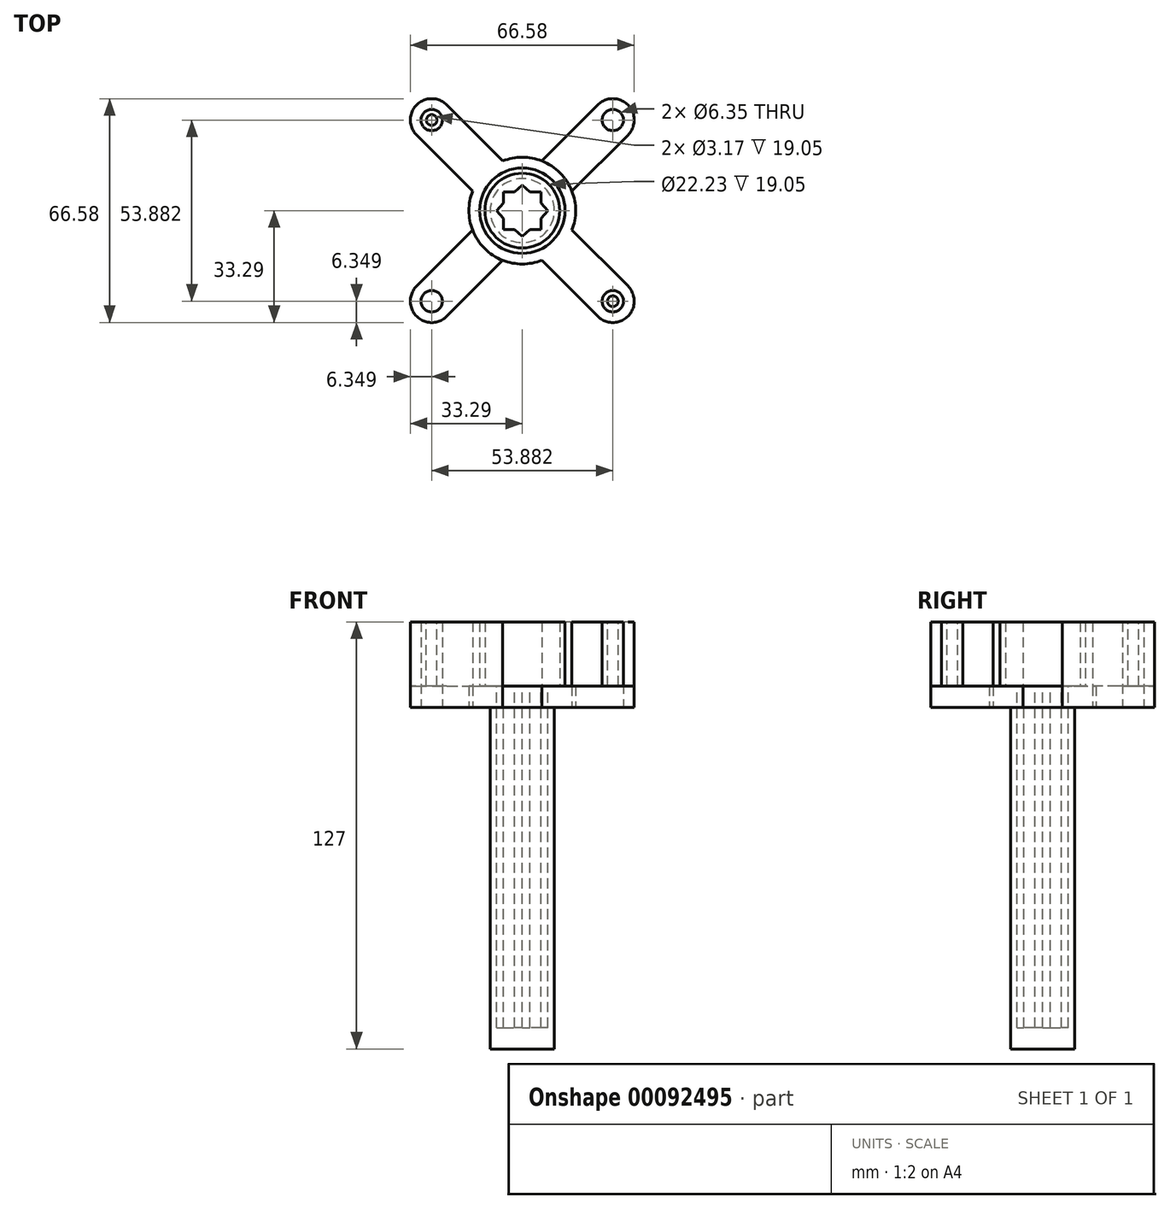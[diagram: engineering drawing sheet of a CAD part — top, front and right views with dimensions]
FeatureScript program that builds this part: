
annotation { "Feature Type Name" : "Feature", "Feature Type Description" : "" }
export const myFeature = defineFeature(function(context is Context, id is Id, definition is map)
    precondition{}
    {
        {
            var Q0;
            Q0=qCreatedBy(makeId("Top.planeOp"),FACE);
            var sketch = newSketch(context, id + "F0", { "sketchPlane" : qUnion([Q0])});
            skCircle(sketch, "E0", {"center": v(0, 0) * mm, "radius": 9.53 * mm});
            skSolve(sketch);
        }
        {
            var Q0;
            Q0 = qSketchRegion(id + "F0", true);
            extrude(context, id + "F1", {"entities" : qUnion([Q0]), "endBound" : BoundingType.SYMMETRIC, "depth" : 101.6 * mm});
        }
        {
            var Q0;
            Q0=makeQuery(id+"F1.opExtrude","CAP_FACE",FACE,{"disambiguationData":[OSD([sQuery(id+"F0.wireOp",EDGE,"E0")])],"isStart":false});
            var sketch = newSketch(context, id + "F2", { "sketchPlane" : qUnion([Q0])});
            skCircle(sketch, "E1", {"center": v(0, 0) * mm, "radius": 15.88 * mm});
            skLineSegment(sketch, "E2", {"start": v(-22.45, 31.43) * mm, "end": v(-5.8, 14.78) * mm});
            skLineSegment(sketch, "E3", {"start": v(-31.43, 22.45) * mm, "end": v(-14.78, 5.8) * mm});
            skLineSegment(sketch, "E4.MirrorCS", {"start": v(31.43, -22.45) * mm, "end": v(14.78, -5.8) * mm});
            skLineSegment(sketch, "E5.MirrorCS", {"start": v(22.45, -31.43) * mm, "end": v(5.8, -14.78) * mm});
            skLineSegment(sketch, "E6", {"start": v(31.43, 22.45) * mm, "end": v(14.78, 5.8) * mm});
            skLineSegment(sketch, "E7.MirrorCS", {"start": v(22.45, 31.43) * mm, "end": v(5.8, 14.78) * mm});
            skLineSegment(sketch, "E8.MirrorCS", {"start": v(-22.45, -31.43) * mm, "end": v(-5.8, -14.78) * mm});
            skLineSegment(sketch, "E9.MirrorCS", {"start": v(-31.43, -22.45) * mm, "end": v(-14.78, -5.8) * mm});
            skArc(sketch, "E10", {"start": v(31.43, 22.45) * mm, "mid": v(31.43, 31.43) * mm, "end": v(22.45, 31.43) * mm});
            skArc(sketch, "E11.MirrorCS", {"start": v(-31.43, 22.45) * mm, "mid": v(-31.43, 31.43) * mm, "end": v(-22.45, 31.43) * mm});
            skArc(sketch, "E12.MirrorCS", {"start": v(-31.43, -22.45) * mm, "mid": v(-31.43, -31.43) * mm, "end": v(-22.45, -31.43) * mm});
            skArc(sketch, "E13.MirrorCS", {"start": v(31.43, -22.45) * mm, "mid": v(31.43, -31.43) * mm, "end": v(22.45, -31.43) * mm});
            skCircle(sketch, "E14", {"center": v(-26.94, 26.94) * mm, "radius": 3.18 * mm});
            skCircle(sketch, "E15.MirrorC", {"center": v(-26.94, -26.94) * mm, "radius": 3.18 * mm});
            skCircle(sketch, "E16.MirrorC", {"center": v(26.94, 26.94) * mm, "radius": 3.18 * mm});
            skCircle(sketch, "E17.MirrorC", {"center": v(26.94, -26.94) * mm, "radius": 3.18 * mm});
            skSolve(sketch);
        }
        {
            var Q0;
            {var subQ0=sQuery(id+"F2.wireOp",EDGE,"E6");Q0=makeQuery(id+"F2.imprint","IMPRINT",FACE,{"disambiguationData":[TD([[makeQuery(id+"F2.imprint","IMPRINT",EDGE,{"derivedFrom":subQ0}),-1.0]])]});}
            var Q1;
            {var subQ0=sQuery(id+"F2.wireOp",EDGE,"E8.MirrorCS");Q1=makeQuery(id+"F2.imprint","IMPRINT",FACE,{"disambiguationData":[TD([[makeQuery(id+"F2.imprint","IMPRINT",EDGE,{"derivedFrom":subQ0}),1.0]])]});}
            var Q2;
            {var subQ0=sQuery(id+"F2.wireOp",EDGE,"E4.MirrorCS");Q2=makeQuery(id+"F2.imprint","IMPRINT",FACE,{"disambiguationData":[TD([[makeQuery(id+"F2.imprint","IMPRINT",EDGE,{"derivedFrom":subQ0}),1.0]])]});}
            var Q3;
            Q3=makeQuery(id+"F2.imprint","IMPRINT",FACE,{"disambiguationData":[TD([[makeQuery(id+"F2.imprint","IMPRINT",EDGE,{"derivedFrom":makeQuery(id+"F1.opExtrude","CAP_EDGE",EDGE,{"disambiguationData":[OSD([sQuery(id+"F0.wireOp",EDGE,"E0")])],"isStart":false})}),1.0]])]});
            var Q4;
            Q4=makeQuery(id+"F2.imprint","IMPRINT",FACE,{"disambiguationData":[TD([[makeQuery(id+"F2.imprint","IMPRINT",EDGE,{"derivedFrom":makeQuery(id+"F1.opExtrude","CAP_EDGE",EDGE,{"disambiguationData":[OSD([sQuery(id+"F0.wireOp",EDGE,"E0")])],"isStart":false})}),-1.0]])]});
            var Q5;
            {var subQ0=sQuery(id+"F2.wireOp",EDGE,"E2");Q5=makeQuery(id+"F2.imprint","IMPRINT",FACE,{"disambiguationData":[TD([[makeQuery(id+"F2.imprint","IMPRINT",EDGE,{"derivedFrom":subQ0}),-1.0]])]});}
            extrude(context, id + "F3", {"entities" : qUnion([Q0, Q1, Q2, Q3, Q4, Q5]), "operationType" : NewBodyOperationType.ADD, "depth" : 6.35 * mm});
        }
        {
            var Q0;
            Q0=makeQuery(id+"F2.imprint","IMPRINT",FACE,{"disambiguationData":[TD([[makeQuery(id+"F2.imprint","IMPRINT",EDGE,{"derivedFrom":sQuery(id+"F2.wireOp",EDGE,"E14")}),1.0]])]});
            var Q1;
            Q1=makeQuery(id+"F2.imprint","IMPRINT",FACE,{"disambiguationData":[TD([[makeQuery(id+"F2.imprint","IMPRINT",EDGE,{"derivedFrom":sQuery(id+"F2.wireOp",EDGE,"E16.MirrorC")}),-1.0]])]});
            var Q2;
            Q2=makeQuery(id+"F2.imprint","IMPRINT",FACE,{"disambiguationData":[TD([[makeQuery(id+"F2.imprint","IMPRINT",EDGE,{"derivedFrom":sQuery(id+"F2.wireOp",EDGE,"E17.MirrorC")}),1.0]])]});
            var Q3;
            Q3=makeQuery(id+"F2.imprint","IMPRINT",FACE,{"disambiguationData":[TD([[makeQuery(id+"F2.imprint","IMPRINT",EDGE,{"derivedFrom":sQuery(id+"F2.wireOp",EDGE,"E15.MirrorC")}),-1.0]])]});
            extrude(context, id + "F4", {"entities" : qUnion([Q0, Q1, Q2, Q3]), "operationType" : NewBodyOperationType.ADD, "depth" : 25.4 * mm});
        }
        {
            var Q0;
            Q0=makeQuery(id+"F3.opExtrude","CAP_FACE",FACE,{"disambiguationData":[OSD([sQuery(id+"F2.wireOp",EDGE,"E1"),sQuery(id+"F2.wireOp",EDGE,"E2"),sQuery(id+"F2.wireOp",EDGE,"E3"),sQuery(id+"F2.wireOp",EDGE,"E4.MirrorCS"),sQuery(id+"F2.wireOp",EDGE,"E5.MirrorCS"),sQuery(id+"F2.wireOp",EDGE,"E6"),sQuery(id+"F2.wireOp",EDGE,"E7.MirrorCS"),sQuery(id+"F2.wireOp",EDGE,"E8.MirrorCS"),sQuery(id+"F2.wireOp",EDGE,"E9.MirrorCS"),sQuery(id+"F2.wireOp",EDGE,"E10"),sQuery(id+"F2.wireOp",EDGE,"E11.MirrorCS"),sQuery(id+"F2.wireOp",EDGE,"E12.MirrorCS"),sQuery(id+"F2.wireOp",EDGE,"E13.MirrorCS"),sQuery(id+"F2.wireOp",EDGE,"E14"),sQuery(id+"F2.wireOp",EDGE,"E15.MirrorC"),sQuery(id+"F2.wireOp",EDGE,"E16.MirrorC"),sQuery(id+"F2.wireOp",EDGE,"E17.MirrorC")])],"isStart":false});
            var sketch = newSketch(context, id + "F5", { "sketchPlane" : qUnion([Q0])});
            skLineSegment(sketch, "E18", {"start": v(-7.62, 0) * mm, "end": v(-7.62, 7.62) * mm});
            skLineSegment(sketch, "E19", {"start": v(-7.62, 7.62) * mm, "end": v(0, 7.62) * mm});
            skLineSegment(sketch, "E20", {"start": v(0, 7.62) * mm, "end": v(-2.28, 5.6) * mm});
            skLineSegment(sketch, "E21", {"start": v(-7.62, 0) * mm, "end": v(-5.6, 2.28) * mm});
            skLineSegment(sketch, "E22", {"start": v(-5.6, 2.28) * mm, "end": v(-5.6, 5.6) * mm});
            skLineSegment(sketch, "E23", {"start": v(-5.6, 5.6) * mm, "end": v(-2.28, 5.6) * mm});
            skLineSegment(sketch, "E24.MirrorCS", {"start": v(7.62, 7.62) * mm, "end": v(0, 7.62) * mm});
            skLineSegment(sketch, "E25.MirrorCS", {"start": v(0, 7.62) * mm, "end": v(2.28, 5.6) * mm});
            skLineSegment(sketch, "E26.MirrorCS", {"start": v(5.6, 5.6) * mm, "end": v(2.28, 5.6) * mm});
            skLineSegment(sketch, "E27.MirrorCS", {"start": v(5.6, 2.28) * mm, "end": v(5.6, 5.6) * mm});
            skLineSegment(sketch, "E28.MirrorCS", {"start": v(7.62, 0) * mm, "end": v(5.6, 2.28) * mm});
            skLineSegment(sketch, "E29.MirrorCS", {"start": v(7.62, 0) * mm, "end": v(7.62, 7.62) * mm});
            skLineSegment(sketch, "E30.MirrorCS", {"start": v(-7.62, 0) * mm, "end": v(-5.6, -2.28) * mm});
            skLineSegment(sketch, "E31.MirrorCS", {"start": v(-5.6, -2.28) * mm, "end": v(-5.6, -5.6) * mm});
            skLineSegment(sketch, "E32.MirrorCS", {"start": v(-5.6, -5.6) * mm, "end": v(-2.28, -5.6) * mm});
            skLineSegment(sketch, "E33.MirrorCS", {"start": v(0, -7.62) * mm, "end": v(-2.28, -5.6) * mm});
            skLineSegment(sketch, "E34.MirrorCS", {"start": v(0, -7.62) * mm, "end": v(2.28, -5.6) * mm});
            skLineSegment(sketch, "E35.MirrorCS", {"start": v(5.6, -5.6) * mm, "end": v(2.28, -5.6) * mm});
            skLineSegment(sketch, "E36.MirrorCS", {"start": v(5.6, -2.28) * mm, "end": v(5.6, -5.6) * mm});
            skLineSegment(sketch, "E37.MirrorCS", {"start": v(7.62, 0) * mm, "end": v(5.6, -2.28) * mm});
            skLineSegment(sketch, "E38.MirrorCS", {"start": v(7.62, 0) * mm, "end": v(7.62, -7.62) * mm});
            skLineSegment(sketch, "E39.MirrorCS", {"start": v(7.62, -7.62) * mm, "end": v(0, -7.62) * mm});
            skLineSegment(sketch, "E40.MirrorCS", {"start": v(-7.62, -7.62) * mm, "end": v(0, -7.62) * mm});
            skLineSegment(sketch, "E41.MirrorCS", {"start": v(-7.62, 0) * mm, "end": v(-7.62, -7.62) * mm});
            skCircle(sketch, "E42", {"center": v(0, 0) * mm, "radius": 11.11 * mm});
            skCircle(sketch, "E43", {"center": v(0, 0) * mm, "radius": 12.7 * mm});
            skSolve(sketch);
        }
        {
            var Q0;
            Q0=makeQuery(id+"F5.imprint","IMPRINT",FACE,{"disambiguationData":[TD([[makeQuery(id+"F5.imprint","IMPRINT",EDGE,{"derivedFrom":sQuery(id+"F5.wireOp",EDGE,"E20")}),1.0]])]});
            extrude(context, id + "F6", {"entities" : qUnion([Q0]), "operationType" : NewBodyOperationType.REMOVE, "oppositeDirection" : true, "depth" : 101.6 * mm});
        }
        {
            var Q0;
            Q0=makeQuery(id+"F5.imprint","IMPRINT",FACE,{"disambiguationData":[TD([[makeQuery(id+"F5.imprint","IMPRINT",EDGE,{"derivedFrom":sQuery(id+"F5.wireOp",EDGE,"E42")}),-1.0]])]});
            extrude(context, id + "F7", {"entities" : qUnion([Q0]), "operationType" : NewBodyOperationType.ADD, "depth" : 19.05 * mm});
        }
        {
            var Q0;
            Q0=makeQuery(id+"F4.opExtrude","CAP_FACE",FACE,{"disambiguationData":[OSD([sQuery(id+"F2.wireOp",EDGE,"E17.MirrorC")])],"isStart":false});
            var sketch = newSketch(context, id + "F8", { "sketchPlane" : qUnion([Q0])});
            skCircle(sketch, "E44", {"center": v(26.94, -26.94) * mm, "radius": 1.59 * mm});
            skCircle(sketch, "E45.MirrorC", {"center": v(-26.94, -26.94) * mm, "radius": 1.59 * mm});
            skCircle(sketch, "E46.MirrorC", {"center": v(26.94, 26.94) * mm, "radius": 1.59 * mm});
            skCircle(sketch, "E47.MirrorC", {"center": v(-26.94, 26.94) * mm, "radius": 1.59 * mm});
            skSolve(sketch);
        }
        {
            var Q0;
            Q0 = qSketchRegion(id + "F8", true);
            extrude(context, id + "F9", {"entities" : qUnion([Q0]), "operationType" : NewBodyOperationType.REMOVE, "oppositeDirection" : true, "depth" : 19.05 * mm});
        }
    });
